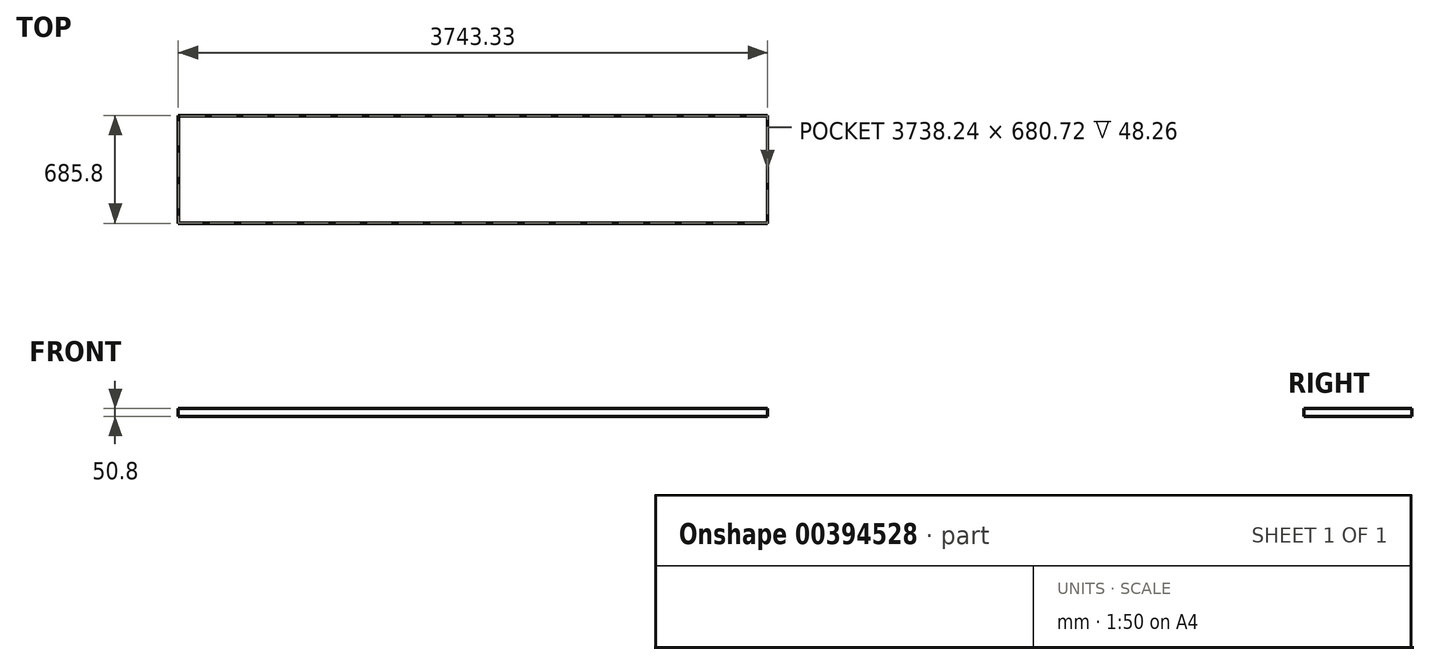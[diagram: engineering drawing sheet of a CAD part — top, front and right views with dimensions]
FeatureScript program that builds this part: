
annotation { "Feature Type Name" : "Feature", "Feature Type Description" : "" }
export const myFeature = defineFeature(function(context is Context, id is Id, definition is map)
    precondition{}
    {
        {
            var Q0;
            Q0=qCreatedBy(makeId("Top.planeOp"),FACE);
            var sketch = newSketch(context, id + "F0", { "sketchPlane" : qUnion([Q0])});
            skLineSegment(sketch, "E0.bottom", {"start": v(-3678.62, 677.27) * mm, "end": v(64.7, 677.27) * mm});
            skLineSegment(sketch, "E0.top", {"start": v(-3678.62, -8.53) * mm, "end": v(64.7, -8.53) * mm});
            skLineSegment(sketch, "E0.left", {"start": v(-3678.62, 677.27) * mm, "end": v(-3678.62, -8.53) * mm});
            skLineSegment(sketch, "E0.right", {"start": v(64.7, 677.27) * mm, "end": v(64.7, -8.53) * mm});
            skLineSegment(sketch, "E1.0", {"start": v(-3677.1, 675.75) * mm, "end": v(63.18, 675.75) * mm});
            skLineSegment(sketch, "E1.1", {"start": v(-3677.1, 675.75) * mm, "end": v(-3677.1, -7) * mm});
            skLineSegment(sketch, "E1.2", {"start": v(-3677.1, -7) * mm, "end": v(63.18, -7) * mm});
            skLineSegment(sketch, "E1.3", {"start": v(63.18, 675.75) * mm, "end": v(63.18, -7) * mm});
            skSolve(sketch);
        }
        {
            var Q0;
            Q0=makeQuery(id+"F0.imprint","IMPRINT",FACE,{"disambiguationData":[TD([[makeQuery(id+"F0.imprint","IMPRINT",EDGE,{"derivedFrom":sQuery(id+"F0.wireOp",EDGE,"E1.0")}),-1.0]])]});
            var Q1;
            Q1=makeQuery(id+"F0.imprint","IMPRINT",FACE,{"disambiguationData":[TD([[makeQuery(id+"F0.imprint","IMPRINT",EDGE,{"derivedFrom":sQuery(id+"F0.wireOp",EDGE,"E0.bottom")}),-1.0]])]});
            extrude(context, id + "F1", {"entities" : qUnion([Q0, Q1]), "depth" : 50.8 * mm});
        }
        {
            var Q0;
            Q0=sQuery(id+"F0.wireOp",EDGE,"E1.2");
            var Q1;
            Q1=sQuery(id+"F0.wireOp",EDGE,"E1.3");
            var Q2;
            Q2=sQuery(id+"F0.wireOp",EDGE,"E1.0");
            var Q3;
            Q3=sQuery(id+"F0.wireOp",EDGE,"E1.1");
            extrude(context, id + "F2", {"bodyType" : ToolBodyType.SURFACE, "surfaceEntities" : qUnion([Q0, Q1, Q2, Q3]), "depth" : 49.28 * mm});
        }
        {
            var Q0;
            Q0=makeQuery(id+"F1.opExtrude","CAP_FACE",FACE,{"disambiguationData":[OSD([sQuery(id+"F0.wireOp",EDGE,"E0.bottom"),sQuery(id+"F0.wireOp",EDGE,"E0.top"),sQuery(id+"F0.wireOp",EDGE,"E0.left"),sQuery(id+"F0.wireOp",EDGE,"E0.right")])],"isStart":false});
            shell(context, id + "F3", {"entities" : qUnion([Q0]), "thickness" : 2.54 * mm});
        }
    });
